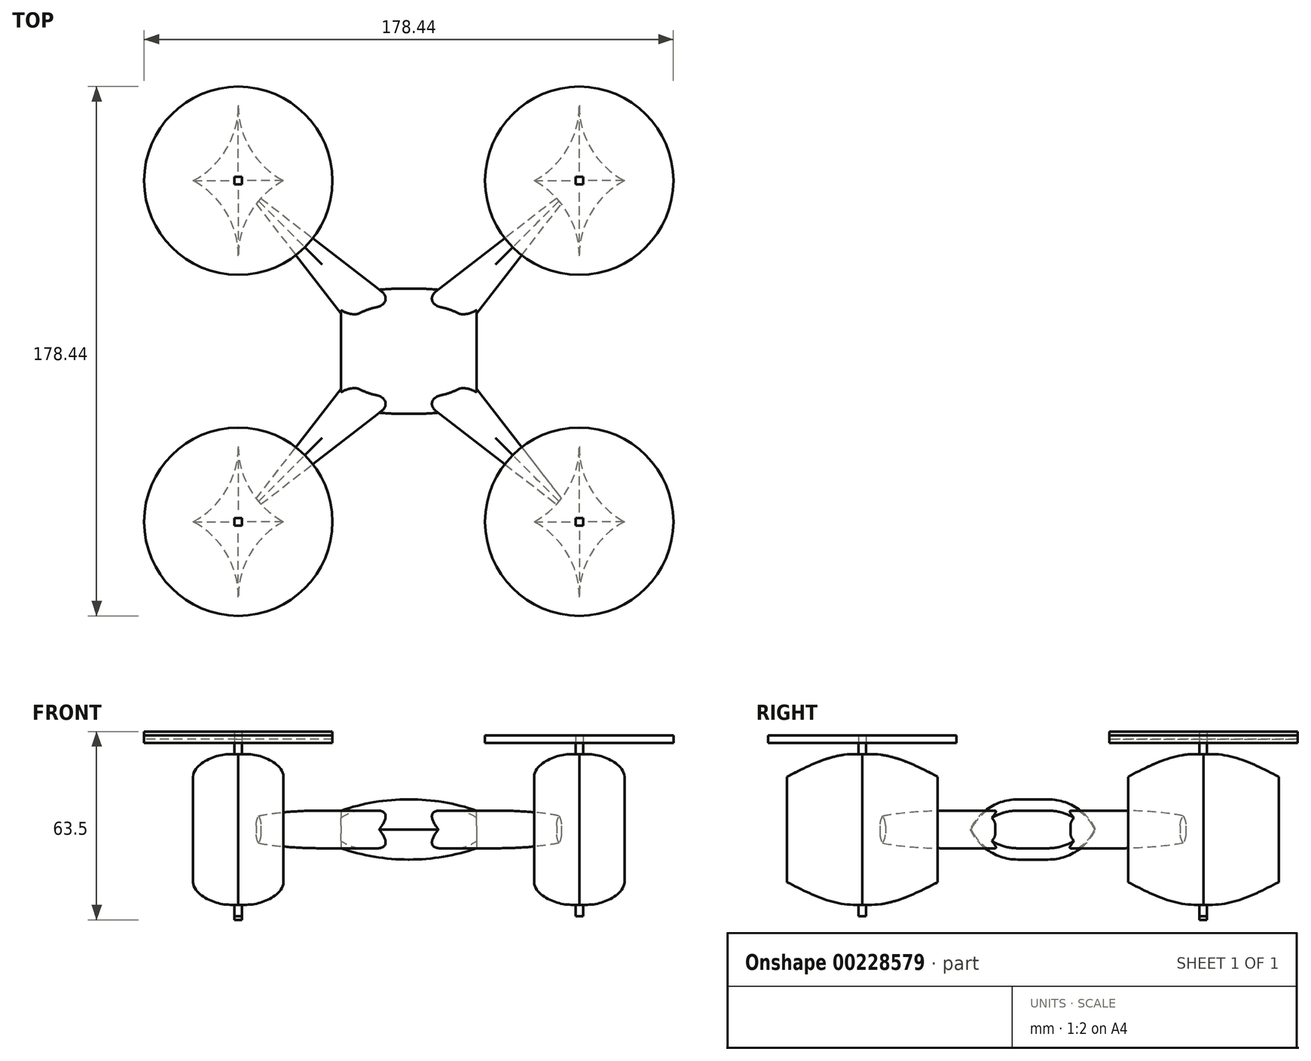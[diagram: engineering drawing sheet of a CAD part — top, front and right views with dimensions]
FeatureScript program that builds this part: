
annotation { "Feature Type Name" : "Feature", "Feature Type Description" : "" }
export const myFeature = defineFeature(function(context is Context, id is Id, definition is map)
    precondition{}
    {
        {
            var Q0;
            Q0=qCreatedBy(makeId("Top.planeOp"),FACE);
            var sketch = newSketch(context, id + "F0", { "sketchPlane" : qUnion([Q0])});
            skLineSegment(sketch, "E0.bottom", {"start": v(22.86, -22.86) * mm, "end": v(-22.86, -22.86) * mm});
            skLineSegment(sketch, "E0.top", {"start": v(22.86, 22.86) * mm, "end": v(-22.86, 22.86) * mm});
            skLineSegment(sketch, "E0.left", {"start": v(22.86, -22.86) * mm, "end": v(22.86, 22.86) * mm});
            skLineSegment(sketch, "E0.right", {"start": v(-22.86, -22.86) * mm, "end": v(-22.86, 22.86) * mm});
            skPoint(sketch, "E0.middle", {"position": v(0, 0) * mm});
            skLineSegment(sketch, "E1", {"start": v(0, 0) * mm, "end": v(-57.47, 57.47) * mm, "construction": true});
            skLineSegment(sketch, "E2", {"start": v(0, 0) * mm, "end": v(57.47, 57.47) * mm, "construction": true});
            skLineSegment(sketch, "E3", {"start": v(0, 0) * mm, "end": v(57.47, -57.47) * mm, "construction": true});
            skLineSegment(sketch, "E4", {"start": v(0, 0) * mm, "end": v(-57.47, -57.47) * mm, "construction": true});
            skLineSegment(sketch, "E5", {"start": v(-57.47, 57.47) * mm, "end": v(-57.47, 82.87) * mm, "construction": true});
            skLineSegment(sketch, "E6", {"start": v(-57.47, 32.07) * mm, "end": v(-57.47, 57.47) * mm, "construction": true});
            skLineSegment(sketch, "E7", {"start": v(-57.47, 57.47) * mm, "end": v(-42.23, 57.47) * mm, "construction": true});
            skLineSegment(sketch, "E8", {"start": v(-57.47, 57.47) * mm, "end": v(-72.71, 57.47) * mm, "construction": true});
            skArc(sketch, "E9", {"start": v(-72.71, 57.47) * mm, "mid": v(-61.58, 68.06) * mm, "end": v(-57.47, 82.87) * mm});
            skArc(sketch, "E10", {"start": v(-57.47, 82.87) * mm, "mid": v(-53.37, 68.06) * mm, "end": v(-42.23, 57.47) * mm});
            skArc(sketch, "E11", {"start": v(-57.47, 32.07) * mm, "mid": v(-61.58, 46.88) * mm, "end": v(-72.71, 57.47) * mm});
            skArc(sketch, "E12", {"start": v(-42.23, 57.47) * mm, "mid": v(-53.37, 46.88) * mm, "end": v(-57.47, 32.07) * mm});
            skLineSegment(sketch, "E13", {"start": v(57.47, 57.47) * mm, "end": v(57.47, 82.87) * mm, "construction": true});
            skLineSegment(sketch, "E14", {"start": v(57.47, 32.07) * mm, "end": v(57.47, 57.47) * mm, "construction": true});
            skLineSegment(sketch, "E15", {"start": v(57.47, 57.47) * mm, "end": v(72.71, 57.47) * mm, "construction": true});
            skLineSegment(sketch, "E16", {"start": v(57.47, 57.47) * mm, "end": v(42.23, 57.47) * mm, "construction": true});
            skArc(sketch, "E17", {"start": v(42.23, 57.47) * mm, "mid": v(53.37, 68.06) * mm, "end": v(57.47, 82.87) * mm});
            skArc(sketch, "E18", {"start": v(57.47, 82.87) * mm, "mid": v(61.58, 68.06) * mm, "end": v(72.71, 57.47) * mm});
            skArc(sketch, "E19", {"start": v(57.47, 32.07) * mm, "mid": v(53.37, 46.88) * mm, "end": v(42.23, 57.47) * mm});
            skArc(sketch, "E20", {"start": v(72.71, 57.47) * mm, "mid": v(61.58, 46.88) * mm, "end": v(57.47, 32.07) * mm});
            skLineSegment(sketch, "E21", {"start": v(57.47, -57.47) * mm, "end": v(57.47, -32.07) * mm, "construction": true});
            skLineSegment(sketch, "E22", {"start": v(57.47, -82.87) * mm, "end": v(57.47, -57.47) * mm, "construction": true});
            skLineSegment(sketch, "E23", {"start": v(57.47, -57.47) * mm, "end": v(72.71, -57.47) * mm, "construction": true});
            skLineSegment(sketch, "E24", {"start": v(57.47, -57.47) * mm, "end": v(42.23, -57.47) * mm, "construction": true});
            skArc(sketch, "E25", {"start": v(42.23, -57.47) * mm, "mid": v(53.37, -46.88) * mm, "end": v(57.47, -32.07) * mm});
            skArc(sketch, "E26", {"start": v(57.47, -32.07) * mm, "mid": v(61.58, -46.88) * mm, "end": v(72.71, -57.47) * mm});
            skArc(sketch, "E27", {"start": v(57.47, -82.87) * mm, "mid": v(53.37, -68.06) * mm, "end": v(42.23, -57.47) * mm});
            skArc(sketch, "E28", {"start": v(72.71, -57.47) * mm, "mid": v(61.58, -68.06) * mm, "end": v(57.47, -82.87) * mm});
            skLineSegment(sketch, "E29", {"start": v(-57.47, -57.47) * mm, "end": v(-57.47, -32.07) * mm, "construction": true});
            skLineSegment(sketch, "E30", {"start": v(-57.47, -82.87) * mm, "end": v(-57.47, -57.47) * mm, "construction": true});
            skLineSegment(sketch, "E31", {"start": v(-57.47, -57.47) * mm, "end": v(-42.23, -57.47) * mm, "construction": true});
            skLineSegment(sketch, "E32", {"start": v(-57.47, -57.47) * mm, "end": v(-72.71, -57.47) * mm, "construction": true});
            skArc(sketch, "E33", {"start": v(-72.71, -57.47) * mm, "mid": v(-61.58, -46.88) * mm, "end": v(-57.47, -32.07) * mm});
            skArc(sketch, "E34", {"start": v(-57.47, -32.07) * mm, "mid": v(-53.37, -46.88) * mm, "end": v(-42.23, -57.47) * mm});
            skArc(sketch, "E35", {"start": v(-57.47, -82.87) * mm, "mid": v(-61.58, -68.06) * mm, "end": v(-72.71, -57.47) * mm});
            skArc(sketch, "E36", {"start": v(-42.23, -57.47) * mm, "mid": v(-53.37, -68.06) * mm, "end": v(-57.47, -82.87) * mm});
            skLineSegment(sketch, "E37", {"start": v(0, 0) * mm, "end": v(-12.67, 22.86) * mm, "construction": true});
            skLineSegment(sketch, "E38", {"start": v(0, 0) * mm, "end": v(-22.86, 12.67) * mm, "construction": true});
            skLineSegment(sketch, "E39", {"start": v(0, 0) * mm, "end": v(12.67, 22.86) * mm, "construction": true});
            skLineSegment(sketch, "E40", {"start": v(0, 0) * mm, "end": v(22.86, 12.67) * mm, "construction": true});
            skLineSegment(sketch, "E41", {"start": v(0, 0) * mm, "end": v(-22.86, -12.67) * mm, "construction": true});
            skLineSegment(sketch, "E42", {"start": v(0, 0) * mm, "end": v(-12.67, -22.86) * mm, "construction": true});
            skLineSegment(sketch, "E43", {"start": v(0, 0) * mm, "end": v(22.86, -12.67) * mm, "construction": true});
            skLineSegment(sketch, "E44", {"start": v(0, 0) * mm, "end": v(12.67, -22.86) * mm, "construction": true});
            skLineSegment(sketch, "E45", {"start": v(-57.47, 57.47) * mm, "end": v(-12.67, 22.86) * mm});
            skLineSegment(sketch, "E46", {"start": v(-57.47, 57.47) * mm, "end": v(-22.86, 12.67) * mm});
            skLineSegment(sketch, "E47", {"start": v(57.47, 57.47) * mm, "end": v(12.67, 22.86) * mm});
            skLineSegment(sketch, "E48", {"start": v(22.86, 12.67) * mm, "end": v(57.47, 57.47) * mm});
            skLineSegment(sketch, "E49", {"start": v(22.86, -12.67) * mm, "end": v(57.47, -57.47) * mm});
            skLineSegment(sketch, "E50", {"start": v(12.67, -22.86) * mm, "end": v(57.47, -57.47) * mm});
            skLineSegment(sketch, "E51", {"start": v(-57.47, -57.47) * mm, "end": v(-22.86, -12.67) * mm});
            skLineSegment(sketch, "E52", {"start": v(-57.47, -57.47) * mm, "end": v(-12.67, -22.86) * mm});
            skLineSegment(sketch, "E53", {"start": v(22.86, 0) * mm, "end": v(-22.86, 0) * mm, "construction": true});
            skLineSegment(sketch, "E54.bottom", {"start": v(-58.74, 56.2) * mm, "end": v(-56.2, 56.2) * mm});
            skLineSegment(sketch, "E54.top", {"start": v(-58.74, 58.74) * mm, "end": v(-56.2, 58.74) * mm});
            skLineSegment(sketch, "E54.left", {"start": v(-58.74, 56.2) * mm, "end": v(-58.74, 58.74) * mm});
            skLineSegment(sketch, "E54.right", {"start": v(-56.2, 56.2) * mm, "end": v(-56.2, 58.74) * mm});
            skPoint(sketch, "E54.middle", {"position": v(-57.47, 57.47) * mm});
            skLineSegment(sketch, "E55.bottom", {"start": v(58.74, 58.74) * mm, "end": v(56.2, 58.74) * mm});
            skLineSegment(sketch, "E55.top", {"start": v(58.74, 56.2) * mm, "end": v(56.2, 56.2) * mm});
            skLineSegment(sketch, "E55.left", {"start": v(58.74, 58.74) * mm, "end": v(58.74, 56.2) * mm});
            skLineSegment(sketch, "E55.right", {"start": v(56.2, 58.74) * mm, "end": v(56.2, 56.2) * mm});
            skPoint(sketch, "E55.middle", {"position": v(57.47, 57.47) * mm});
            skLineSegment(sketch, "E56.bottom", {"start": v(58.74, -58.74) * mm, "end": v(56.2, -58.74) * mm});
            skLineSegment(sketch, "E56.top", {"start": v(58.74, -56.2) * mm, "end": v(56.2, -56.2) * mm});
            skLineSegment(sketch, "E56.left", {"start": v(58.74, -58.74) * mm, "end": v(58.74, -56.2) * mm});
            skLineSegment(sketch, "E56.right", {"start": v(56.2, -58.74) * mm, "end": v(56.2, -56.2) * mm});
            skPoint(sketch, "E56.middle", {"position": v(57.47, -57.47) * mm});
            skLineSegment(sketch, "E57.bottom", {"start": v(-58.74, -58.74) * mm, "end": v(-56.2, -58.74) * mm});
            skLineSegment(sketch, "E57.top", {"start": v(-58.74, -56.2) * mm, "end": v(-56.2, -56.2) * mm});
            skLineSegment(sketch, "E57.left", {"start": v(-58.74, -58.74) * mm, "end": v(-58.74, -56.2) * mm});
            skLineSegment(sketch, "E57.right", {"start": v(-56.2, -58.74) * mm, "end": v(-56.2, -56.2) * mm});
            skPoint(sketch, "E57.middle", {"position": v(-57.47, -57.47) * mm});
            skSolve(sketch);
        }
        {
            var Q0;
            {var subQ0=sQuery(id+"F0.wireOp",EDGE,"E0.left");var subQ3=sQuery(id+"F0.wireOp",EDGE,"E0.bottom");var subQ4=makeQuery(id+"F0.imprint","INTERSECT",VERTEX,{"derivedFrom":[subQ3,subQ0]});Q0=makeQuery(id+"F0.imprint","IMPRINT",FACE,{"disambiguationData":[TD([[makeQuery(id+"F0.imprint","IMPRINT",EDGE,{"disambiguationData":[TD([[subQ4,-1.0]])],"derivedFrom":subQ3}),-1.0]])]});}
            extrude(context, id + "F1", {"entities" : qUnion([Q0]), "endBound" : BoundingType.SYMMETRIC, "depth" : 20.32 * mm});
        }
        {
            var Q0;
            {var subQ5=sQuery(id+"F0.wireOp",EDGE,"E0.right");var subQ6=sQuery(id+"F0.wireOp",EDGE,"E0.top");var subQ7=makeQuery(id+"F0.imprint","INTERSECT",VERTEX,{"derivedFrom":[subQ6,subQ5]});Q0=makeQuery(id+"F0.imprint","IMPRINT",FACE,{"disambiguationData":[TD([[makeQuery(id+"F0.imprint","IMPRINT",EDGE,{"disambiguationData":[TD([[subQ7,1.0]])],"derivedFrom":subQ6}),-1.0]])]});}
            var Q1;
            {var subQ5=sQuery(id+"F0.wireOp",EDGE,"E0.left");var subQ6=sQuery(id+"F0.wireOp",EDGE,"E0.top");var subQ7=makeQuery(id+"F0.imprint","INTERSECT",VERTEX,{"derivedFrom":[subQ6,subQ5]});Q1=makeQuery(id+"F0.imprint","IMPRINT",FACE,{"disambiguationData":[TD([[makeQuery(id+"F0.imprint","IMPRINT",EDGE,{"disambiguationData":[TD([[subQ7,-1.0]])],"derivedFrom":subQ6}),-1.0]])]});}
            var Q2;
            {var subQ1=sQuery(id+"F0.wireOp",EDGE,"E0.left");var subQ5=sQuery(id+"F0.wireOp",EDGE,"E0.bottom");var subQ6=makeQuery(id+"F0.imprint","INTERSECT",VERTEX,{"derivedFrom":[subQ5,subQ1]});Q2=makeQuery(id+"F0.imprint","IMPRINT",FACE,{"disambiguationData":[TD([[makeQuery(id+"F0.imprint","IMPRINT",EDGE,{"disambiguationData":[TD([[subQ6,-1.0]])],"derivedFrom":subQ5}),1.0]])]});}
            var Q3;
            {var subQ1=sQuery(id+"F0.wireOp",EDGE,"E0.right");var subQ5=sQuery(id+"F0.wireOp",EDGE,"E0.bottom");var subQ6=makeQuery(id+"F0.imprint","INTERSECT",VERTEX,{"derivedFrom":[subQ5,subQ1]});Q3=makeQuery(id+"F0.imprint","IMPRINT",FACE,{"disambiguationData":[TD([[makeQuery(id+"F0.imprint","IMPRINT",EDGE,{"disambiguationData":[TD([[subQ6,1.0]])],"derivedFrom":subQ5}),1.0]])]});}
            extrude(context, id + "F2", {"entities" : qUnion([Q0, Q1, Q2, Q3]), "operationType" : NewBodyOperationType.ADD, "endBound" : BoundingType.SYMMETRIC, "depth" : 12.7 * mm});
        }
        {
            var Q0;
            Q0=makeQuery(id+"F0.imprint","IMPRINT",FACE,{"disambiguationData":[TD([[makeQuery(id+"F0.imprint","IMPRINT",EDGE,{"derivedFrom":sQuery(id+"F0.wireOp",EDGE,"E9")}),-1.0]])]});
            var Q1;
            {var subQ0=sQuery(id+"F0.wireOp",EDGE,"E45");var subQ1=sQuery(id+"F0.wireOp",EDGE,"E12");var subQ2=makeQuery(id+"F0.imprint","INTERSECT",VERTEX,{"derivedFrom":[subQ1,subQ0]});Q1=makeQuery(id+"F0.imprint","IMPRINT",FACE,{"disambiguationData":[TD([[makeQuery(id+"F0.imprint","IMPRINT",EDGE,{"disambiguationData":[TD([[subQ2,-1.0]])],"derivedFrom":subQ1}),-1.0]])]});}
            var Q2;
            {var subQ1=sQuery(id+"F0.wireOp",EDGE,"E17");Q2=makeQuery(id+"F0.imprint","IMPRINT",FACE,{"disambiguationData":[TD([[makeQuery(id+"F0.imprint","IMPRINT",EDGE,{"derivedFrom":subQ1}),-1.0]])]});}
            var Q3;
            {var subQ0=sQuery(id+"F0.wireOp",EDGE,"E48");var subQ1=sQuery(id+"F0.wireOp",EDGE,"E19");var subQ2=makeQuery(id+"F0.imprint","INTERSECT",VERTEX,{"derivedFrom":[subQ1,subQ0]});Q3=makeQuery(id+"F0.imprint","IMPRINT",FACE,{"disambiguationData":[TD([[makeQuery(id+"F0.imprint","IMPRINT",EDGE,{"disambiguationData":[TD([[subQ2,-1.0]])],"derivedFrom":subQ1}),-1.0]])]});}
            var Q4;
            {var subQ1=sQuery(id+"F0.wireOp",EDGE,"E26");Q4=makeQuery(id+"F0.imprint","IMPRINT",FACE,{"disambiguationData":[TD([[makeQuery(id+"F0.imprint","IMPRINT",EDGE,{"derivedFrom":subQ1}),-1.0]])]});}
            var Q5;
            {var subQ0=sQuery(id+"F0.wireOp",EDGE,"E50");var subQ1=sQuery(id+"F0.wireOp",EDGE,"E25");var subQ2=makeQuery(id+"F0.imprint","INTERSECT",VERTEX,{"derivedFrom":[subQ1,subQ0]});Q5=makeQuery(id+"F0.imprint","IMPRINT",FACE,{"disambiguationData":[TD([[makeQuery(id+"F0.imprint","IMPRINT",EDGE,{"disambiguationData":[TD([[subQ2,-1.0]])],"derivedFrom":subQ1}),-1.0]])]});}
            var Q6;
            {var subQ4=sQuery(id+"F0.wireOp",EDGE,"E33");Q6=makeQuery(id+"F0.imprint","IMPRINT",FACE,{"disambiguationData":[TD([[makeQuery(id+"F0.imprint","IMPRINT",EDGE,{"derivedFrom":subQ4}),-1.0]])]});}
            var Q7;
            {var subQ0=sQuery(id+"F0.wireOp",EDGE,"E51");var subQ1=sQuery(id+"F0.wireOp",EDGE,"E34");var subQ2=makeQuery(id+"F0.imprint","INTERSECT",VERTEX,{"derivedFrom":[subQ1,subQ0]});Q7=makeQuery(id+"F0.imprint","IMPRINT",FACE,{"disambiguationData":[TD([[makeQuery(id+"F0.imprint","IMPRINT",EDGE,{"disambiguationData":[TD([[subQ2,-1.0]])],"derivedFrom":subQ1}),-1.0]])]});}
            extrude(context, id + "F3", {"entities" : qUnion([Q0, Q1, Q2, Q3, Q4, Q5, Q6, Q7]), "operationType" : NewBodyOperationType.ADD, "endBound" : BoundingType.SYMMETRIC, "depth" : 50.8 * mm});
        }
        {
            var Q0;
            Q0=makeQuery(id+"F2.opExtrude","CAP_EDGE",EDGE,{"disambiguationData":[OSD([sQuery(id+"F0.wireOp",EDGE,"E50")])],"isStart":false});
            var Q1;
            Q1=makeQuery(id+"F2.opExtrude","CAP_EDGE",EDGE,{"disambiguationData":[OSD([sQuery(id+"F0.wireOp",EDGE,"E49")])],"isStart":false});
            var Q2;
            Q2=makeQuery(id+"F2.opExtrude","CAP_EDGE",EDGE,{"disambiguationData":[OSD([sQuery(id+"F0.wireOp",EDGE,"E50")])],"isStart":true});
            var Q3;
            Q3=makeQuery(id+"F2.opExtrude","CAP_EDGE",EDGE,{"disambiguationData":[OSD([sQuery(id+"F0.wireOp",EDGE,"E49")])],"isStart":true});
            fillet(context, id + "F4", {"entities" : qUnion([Q0, Q1, Q2, Q3]), "radius" : 5.08 * mm, "tangentPropagation" : true, "allowEdgeOverflow" : false});
        }
        {
            var Q0;
            Q0=makeQuery(id+"F2.opExtrude","CAP_EDGE",EDGE,{"disambiguationData":[OSD([sQuery(id+"F0.wireOp",EDGE,"E52")])],"isStart":false});
            var Q1;
            Q1=makeQuery(id+"F2.opExtrude","CAP_EDGE",EDGE,{"disambiguationData":[OSD([sQuery(id+"F0.wireOp",EDGE,"E51")])],"isStart":false});
            var Q2;
            Q2=makeQuery(id+"F2.opExtrude","CAP_EDGE",EDGE,{"disambiguationData":[OSD([sQuery(id+"F0.wireOp",EDGE,"E51")])],"isStart":true});
            var Q3;
            Q3=makeQuery(id+"F2.opExtrude","CAP_EDGE",EDGE,{"disambiguationData":[OSD([sQuery(id+"F0.wireOp",EDGE,"E52")])],"isStart":true});
            var Q4;
            Q4=makeQuery(id+"F2.opExtrude","CAP_EDGE",EDGE,{"disambiguationData":[OSD([sQuery(id+"F0.wireOp",EDGE,"E48")])],"isStart":false});
            var Q5;
            Q5=makeQuery(id+"F2.opExtrude","CAP_EDGE",EDGE,{"disambiguationData":[OSD([sQuery(id+"F0.wireOp",EDGE,"E47")])],"isStart":false});
            var Q6;
            Q6=makeQuery(id+"F2.opExtrude","CAP_EDGE",EDGE,{"disambiguationData":[OSD([sQuery(id+"F0.wireOp",EDGE,"E48")])],"isStart":true});
            var Q7;
            Q7=makeQuery(id+"F2.opExtrude","CAP_EDGE",EDGE,{"disambiguationData":[OSD([sQuery(id+"F0.wireOp",EDGE,"E47")])],"isStart":true});
            var Q8;
            Q8=makeQuery(id+"F2.opExtrude","CAP_EDGE",EDGE,{"disambiguationData":[OSD([sQuery(id+"F0.wireOp",EDGE,"E45")])],"isStart":true});
            var Q9;
            Q9=makeQuery(id+"F2.opExtrude","CAP_EDGE",EDGE,{"disambiguationData":[OSD([sQuery(id+"F0.wireOp",EDGE,"E46")])],"isStart":true});
            var Q10;
            Q10=makeQuery(id+"F2.opExtrude","CAP_EDGE",EDGE,{"disambiguationData":[OSD([sQuery(id+"F0.wireOp",EDGE,"E46")])],"isStart":false});
            var Q11;
            Q11=makeQuery(id+"F2.opExtrude","CAP_EDGE",EDGE,{"disambiguationData":[OSD([sQuery(id+"F0.wireOp",EDGE,"E45")])],"isStart":false});
            fillet(context, id + "F5", {"entities" : qUnion([Q0, Q1, Q2, Q3, Q4, Q5, Q6, Q7, Q8, Q9, Q10, Q11]), "radius" : 5.08 * mm, "tangentPropagation" : true, "allowEdgeOverflow" : false});
        }
        {
            var Q0;
            Q0=makeQuery(id+"F1.opExtrude","CAP_EDGE",EDGE,{"disambiguationData":[OSD([sQuery(id+"F0.wireOp",EDGE,"E0.right")])],"isStart":true});
            var Q1;
            Q1=makeQuery(id+"F1.opExtrude","CAP_EDGE",EDGE,{"disambiguationData":[OSD([sQuery(id+"F0.wireOp",EDGE,"E0.right")])],"isStart":false});
            fillet(context, id + "F6", {"entities" : qUnion([Q0, Q1]), "radius" : 69.9 * mm, "tangentPropagation" : true, "allowEdgeOverflow" : false});
        }
        {
            var Q0;
            Q0=makeQuery(id+"F1.opExtrude","CAP_EDGE",EDGE,{"disambiguationData":[OSD([sQuery(id+"F0.wireOp",EDGE,"E0.left")])],"isStart":true});
            var Q1;
            Q1=makeQuery(id+"F1.opExtrude","CAP_EDGE",EDGE,{"disambiguationData":[OSD([sQuery(id+"F0.wireOp",EDGE,"E0.left")])],"isStart":false});
            fillet(context, id + "F7", {"entities" : qUnion([Q0, Q1]), "radius" : 69.9 * mm, "tangentPropagation" : true, "allowEdgeOverflow" : false});
        }
        {
            var Q0;
            Q0=makeQuery(id+"F6.opFillet","BLEND_EDGE",EDGE,{"blendedFrom":[makeQuery(id+"F1.opExtrude","CAP_EDGE",EDGE,{"disambiguationData":[OSD([sQuery(id+"F0.wireOp",EDGE,"E0.right")])],"isStart":false}),makeQuery(id+"F1.opExtrude","SWEPT_FACE",FACE,{"disambiguationData":[OSD([sQuery(id+"F0.wireOp",EDGE,"E0.bottom")])]})],"blendedInto":[makeQuery(id+"F1.opExtrude","SWEPT_FACE",FACE,{"disambiguationData":[OSD([sQuery(id+"F0.wireOp",EDGE,"E0.bottom")])]})]});
            var Q1;
            Q1=makeQuery(id+"F7.opFillet","BLEND_EDGE",EDGE,{"blendedFrom":[makeQuery(id+"F1.opExtrude","CAP_EDGE",EDGE,{"disambiguationData":[OSD([sQuery(id+"F0.wireOp",EDGE,"E0.left")])],"isStart":false}),makeQuery(id+"F1.opExtrude","SWEPT_FACE",FACE,{"disambiguationData":[OSD([sQuery(id+"F0.wireOp",EDGE,"E0.bottom")])]})],"blendedInto":[makeQuery(id+"F1.opExtrude","SWEPT_FACE",FACE,{"disambiguationData":[OSD([sQuery(id+"F0.wireOp",EDGE,"E0.bottom")])]})]});
            var Q2;
            Q2=makeQuery(id+"F7.opFillet","BLEND_EDGE",EDGE,{"blendedFrom":[makeQuery(id+"F1.opExtrude","CAP_EDGE",EDGE,{"disambiguationData":[OSD([sQuery(id+"F0.wireOp",EDGE,"E0.left")])],"isStart":true}),makeQuery(id+"F1.opExtrude","SWEPT_FACE",FACE,{"disambiguationData":[OSD([sQuery(id+"F0.wireOp",EDGE,"E0.bottom")])]})],"blendedInto":[makeQuery(id+"F1.opExtrude","SWEPT_FACE",FACE,{"disambiguationData":[OSD([sQuery(id+"F0.wireOp",EDGE,"E0.bottom")])]})]});
            var Q3;
            Q3=makeQuery(id+"F6.opFillet","BLEND_EDGE",EDGE,{"blendedFrom":[makeQuery(id+"F1.opExtrude","CAP_EDGE",EDGE,{"disambiguationData":[OSD([sQuery(id+"F0.wireOp",EDGE,"E0.right")])],"isStart":true}),makeQuery(id+"F1.opExtrude","SWEPT_FACE",FACE,{"disambiguationData":[OSD([sQuery(id+"F0.wireOp",EDGE,"E0.bottom")])]})],"blendedInto":[makeQuery(id+"F1.opExtrude","SWEPT_FACE",FACE,{"disambiguationData":[OSD([sQuery(id+"F0.wireOp",EDGE,"E0.bottom")])]})]});
            fillet(context, id + "F8", {"entities" : qUnion([Q0, Q1, Q2, Q3]), "radius" : 17.78 * mm, "tangentPropagation" : true, "allowEdgeOverflow" : false});
        }
        {
            var Q0;
            Q0=makeQuery(id+"F7.opFillet","BLEND_EDGE",EDGE,{"blendedFrom":[makeQuery(id+"F1.opExtrude","CAP_EDGE",EDGE,{"disambiguationData":[OSD([sQuery(id+"F0.wireOp",EDGE,"E0.left")])],"isStart":true}),makeQuery(id+"F1.opExtrude","SWEPT_FACE",FACE,{"disambiguationData":[OSD([sQuery(id+"F0.wireOp",EDGE,"E0.top")])]})],"blendedInto":[makeQuery(id+"F1.opExtrude","SWEPT_FACE",FACE,{"disambiguationData":[OSD([sQuery(id+"F0.wireOp",EDGE,"E0.top")])]})]});
            var Q1;
            Q1=makeQuery(id+"F6.opFillet","BLEND_EDGE",EDGE,{"blendedFrom":[makeQuery(id+"F1.opExtrude","CAP_EDGE",EDGE,{"disambiguationData":[OSD([sQuery(id+"F0.wireOp",EDGE,"E0.right")])],"isStart":false}),makeQuery(id+"F1.opExtrude","SWEPT_FACE",FACE,{"disambiguationData":[OSD([sQuery(id+"F0.wireOp",EDGE,"E0.top")])]})],"blendedInto":[makeQuery(id+"F1.opExtrude","SWEPT_FACE",FACE,{"disambiguationData":[OSD([sQuery(id+"F0.wireOp",EDGE,"E0.top")])]})]});
            var Q2;
            Q2=makeQuery(id+"F7.opFillet","BLEND_EDGE",EDGE,{"blendedFrom":[makeQuery(id+"F1.opExtrude","CAP_EDGE",EDGE,{"disambiguationData":[OSD([sQuery(id+"F0.wireOp",EDGE,"E0.left")])],"isStart":false}),makeQuery(id+"F1.opExtrude","SWEPT_FACE",FACE,{"disambiguationData":[OSD([sQuery(id+"F0.wireOp",EDGE,"E0.top")])]})],"blendedInto":[makeQuery(id+"F1.opExtrude","SWEPT_FACE",FACE,{"disambiguationData":[OSD([sQuery(id+"F0.wireOp",EDGE,"E0.top")])]})]});
            fillet(context, id + "F9", {"entities" : qUnion([Q0, Q1, Q2]), "radius" : 17.78 * mm, "tangentPropagation" : true, "allowEdgeOverflow" : false});
        }
        {
            var Q0;
            Q0=makeQuery(id+"F3.opExtrude","CAP_EDGE",EDGE,{"disambiguationData":[OSD([sQuery(id+"F0.wireOp",EDGE,"E9")])],"isStart":false});
            var Q1;
            Q1=makeQuery(id+"F3.opExtrude","CAP_EDGE",EDGE,{"disambiguationData":[OSD([sQuery(id+"F0.wireOp",EDGE,"E10")])],"isStart":false});
            var Q2;
            Q2=makeQuery(id+"F3.opExtrude","CAP_EDGE",EDGE,{"disambiguationData":[OSD([sQuery(id+"F0.wireOp",EDGE,"E12")])],"isStart":false});
            var Q3;
            Q3=makeQuery(id+"F3.opExtrude","CAP_EDGE",EDGE,{"disambiguationData":[OSD([sQuery(id+"F0.wireOp",EDGE,"E11")])],"isStart":false});
            fillet(context, id + "F10", {"entities" : qUnion([Q0, Q1, Q2, Q3]), "radius" : 7.62 * mm, "tangentPropagation" : true, "allowEdgeOverflow" : false});
        }
        {
            var Q0;
            Q0=makeQuery(id+"F3.opExtrude","CAP_EDGE",EDGE,{"disambiguationData":[OSD([sQuery(id+"F0.wireOp",EDGE,"E17")])],"isStart":false});
            var Q1;
            Q1=makeQuery(id+"F3.opExtrude","CAP_EDGE",EDGE,{"disambiguationData":[OSD([sQuery(id+"F0.wireOp",EDGE,"E18")])],"isStart":false});
            var Q2;
            Q2=makeQuery(id+"F3.opExtrude","CAP_EDGE",EDGE,{"disambiguationData":[OSD([sQuery(id+"F0.wireOp",EDGE,"E19")])],"isStart":false});
            var Q3;
            Q3=makeQuery(id+"F3.opExtrude","CAP_EDGE",EDGE,{"disambiguationData":[OSD([sQuery(id+"F0.wireOp",EDGE,"E20")])],"isStart":false});
            var Q4;
            Q4=makeQuery(id+"F3.opExtrude","CAP_EDGE",EDGE,{"disambiguationData":[OSD([sQuery(id+"F0.wireOp",EDGE,"E25")])],"isStart":false});
            var Q5;
            Q5=makeQuery(id+"F3.opExtrude","CAP_EDGE",EDGE,{"disambiguationData":[OSD([sQuery(id+"F0.wireOp",EDGE,"E26")])],"isStart":false});
            var Q6;
            Q6=makeQuery(id+"F3.opExtrude","CAP_EDGE",EDGE,{"disambiguationData":[OSD([sQuery(id+"F0.wireOp",EDGE,"E28")])],"isStart":false});
            var Q7;
            Q7=makeQuery(id+"F3.opExtrude","CAP_EDGE",EDGE,{"disambiguationData":[OSD([sQuery(id+"F0.wireOp",EDGE,"E27")])],"isStart":false});
            var Q8;
            Q8=makeQuery(id+"F3.opExtrude","CAP_EDGE",EDGE,{"disambiguationData":[OSD([sQuery(id+"F0.wireOp",EDGE,"E34")])],"isStart":false});
            var Q9;
            Q9=makeQuery(id+"F3.opExtrude","CAP_EDGE",EDGE,{"disambiguationData":[OSD([sQuery(id+"F0.wireOp",EDGE,"E33")])],"isStart":false});
            var Q10;
            Q10=makeQuery(id+"F3.opExtrude","CAP_EDGE",EDGE,{"disambiguationData":[OSD([sQuery(id+"F0.wireOp",EDGE,"E35")])],"isStart":false});
            var Q11;
            Q11=makeQuery(id+"F3.opExtrude","CAP_EDGE",EDGE,{"disambiguationData":[OSD([sQuery(id+"F0.wireOp",EDGE,"E36")])],"isStart":false});
            fillet(context, id + "F11", {"entities" : qUnion([Q0, Q1, Q2, Q3, Q4, Q5, Q6, Q7, Q8, Q9, Q10, Q11]), "radius" : 7.62 * mm, "tangentPropagation" : true, "allowEdgeOverflow" : false});
        }
        {
            var Q0;
            Q0=makeQuery(id+"F3.opExtrude","CAP_EDGE",EDGE,{"disambiguationData":[OSD([sQuery(id+"F0.wireOp",EDGE,"E33")])],"isStart":true});
            var Q1;
            Q1=makeQuery(id+"F3.opExtrude","CAP_EDGE",EDGE,{"disambiguationData":[OSD([sQuery(id+"F0.wireOp",EDGE,"E34")])],"isStart":true});
            var Q2;
            Q2=makeQuery(id+"F3.opExtrude","CAP_EDGE",EDGE,{"disambiguationData":[OSD([sQuery(id+"F0.wireOp",EDGE,"E35")])],"isStart":true});
            var Q3;
            Q3=makeQuery(id+"F3.opExtrude","CAP_EDGE",EDGE,{"disambiguationData":[OSD([sQuery(id+"F0.wireOp",EDGE,"E36")])],"isStart":true});
            fillet(context, id + "F12", {"entities" : qUnion([Q0, Q1, Q2, Q3]), "radius" : 7.62 * mm, "tangentPropagation" : true, "allowEdgeOverflow" : false});
        }
        {
            var Q0;
            Q0=makeQuery(id+"F3.opExtrude","CAP_EDGE",EDGE,{"disambiguationData":[OSD([sQuery(id+"F0.wireOp",EDGE,"E27")])],"isStart":true});
            var Q1;
            Q1=makeQuery(id+"F3.opExtrude","CAP_EDGE",EDGE,{"disambiguationData":[OSD([sQuery(id+"F0.wireOp",EDGE,"E28")])],"isStart":true});
            var Q2;
            Q2=makeQuery(id+"F3.opExtrude","CAP_EDGE",EDGE,{"disambiguationData":[OSD([sQuery(id+"F0.wireOp",EDGE,"E26")])],"isStart":true});
            var Q3;
            Q3=makeQuery(id+"F3.opExtrude","CAP_EDGE",EDGE,{"disambiguationData":[OSD([sQuery(id+"F0.wireOp",EDGE,"E25")])],"isStart":true});
            var Q4;
            Q4=makeQuery(id+"F3.opExtrude","CAP_EDGE",EDGE,{"disambiguationData":[OSD([sQuery(id+"F0.wireOp",EDGE,"E20")])],"isStart":true});
            var Q5;
            Q5=makeQuery(id+"F3.opExtrude","CAP_EDGE",EDGE,{"disambiguationData":[OSD([sQuery(id+"F0.wireOp",EDGE,"E19")])],"isStart":true});
            var Q6;
            Q6=makeQuery(id+"F3.opExtrude","CAP_EDGE",EDGE,{"disambiguationData":[OSD([sQuery(id+"F0.wireOp",EDGE,"E17")])],"isStart":true});
            var Q7;
            Q7=makeQuery(id+"F3.opExtrude","CAP_EDGE",EDGE,{"disambiguationData":[OSD([sQuery(id+"F0.wireOp",EDGE,"E18")])],"isStart":true});
            var Q8;
            Q8=makeQuery(id+"F3.opExtrude","CAP_EDGE",EDGE,{"disambiguationData":[OSD([sQuery(id+"F0.wireOp",EDGE,"E12")])],"isStart":true});
            var Q9;
            Q9=makeQuery(id+"F3.opExtrude","CAP_EDGE",EDGE,{"disambiguationData":[OSD([sQuery(id+"F0.wireOp",EDGE,"E11")])],"isStart":true});
            var Q10;
            Q10=makeQuery(id+"F3.opExtrude","CAP_EDGE",EDGE,{"disambiguationData":[OSD([sQuery(id+"F0.wireOp",EDGE,"E9")])],"isStart":true});
            var Q11;
            Q11=makeQuery(id+"F3.opExtrude","CAP_EDGE",EDGE,{"disambiguationData":[OSD([sQuery(id+"F0.wireOp",EDGE,"E10")])],"isStart":true});
            fillet(context, id + "F13", {"entities" : qUnion([Q0, Q1, Q2, Q3, Q4, Q5, Q6, Q7, Q8, Q9, Q10, Q11]), "radius" : 7.62 * mm, "tangentPropagation" : true, "allowEdgeOverflow" : false});
        }
        {
            var Q0;
            {var subQ0=sQuery(id+"F0.wireOp",EDGE,"E54.top");Q0=makeQuery(id+"F0.imprint","IMPRINT",FACE,{"disambiguationData":[TD([[makeQuery(id+"F0.imprint","IMPRINT",EDGE,{"derivedFrom":subQ0}),-1.0]])]});}
            var Q1;
            {var subQ0=sQuery(id+"F0.wireOp",EDGE,"E46");var subQ1=sQuery(id+"F0.wireOp",EDGE,"E45");var subQ2=makeQuery(id+"F0.imprint","INTERSECT",VERTEX,{"derivedFrom":[subQ1,subQ0]});Q1=makeQuery(id+"F0.imprint","IMPRINT",FACE,{"disambiguationData":[TD([[makeQuery(id+"F0.imprint","IMPRINT",EDGE,{"disambiguationData":[TD([[subQ2,-1.0]])],"derivedFrom":subQ1}),-1.0]])]});}
            extrude(context, id + "F14", {"entities" : qUnion([Q0, Q1]), "operationType" : NewBodyOperationType.ADD, "endBound" : BoundingType.SYMMETRIC, "depth" : 60.96 * mm});
        }
        {
            var Q0;
            {var subQ4=sQuery(id+"F0.wireOp",EDGE,"E57.bottom");Q0=makeQuery(id+"F0.imprint","IMPRINT",FACE,{"disambiguationData":[TD([[makeQuery(id+"F0.imprint","IMPRINT",EDGE,{"derivedFrom":subQ4}),1.0]])]});}
            var Q1;
            {var subQ0=sQuery(id+"F0.wireOp",EDGE,"E52");var subQ1=sQuery(id+"F0.wireOp",EDGE,"E51");var subQ2=makeQuery(id+"F0.imprint","INTERSECT",VERTEX,{"derivedFrom":[subQ1,subQ0]});Q1=makeQuery(id+"F0.imprint","IMPRINT",FACE,{"disambiguationData":[TD([[makeQuery(id+"F0.imprint","IMPRINT",EDGE,{"disambiguationData":[TD([[subQ2,-1.0]])],"derivedFrom":subQ1}),-1.0]])]});}
            var Q2;
            {var subQ4=sQuery(id+"F0.wireOp",EDGE,"E56.bottom");Q2=makeQuery(id+"F0.imprint","IMPRINT",FACE,{"disambiguationData":[TD([[makeQuery(id+"F0.imprint","IMPRINT",EDGE,{"derivedFrom":subQ4}),-1.0]])]});}
            var Q3;
            {var subQ0=sQuery(id+"F0.wireOp",EDGE,"E50");var subQ1=sQuery(id+"F0.wireOp",EDGE,"E49");var subQ2=makeQuery(id+"F0.imprint","INTERSECT",VERTEX,{"derivedFrom":[subQ1,subQ0]});Q3=makeQuery(id+"F0.imprint","IMPRINT",FACE,{"disambiguationData":[TD([[makeQuery(id+"F0.imprint","IMPRINT",EDGE,{"disambiguationData":[TD([[subQ2,1.0]])],"derivedFrom":subQ1}),-1.0]])]});}
            var Q4;
            {var subQ4=sQuery(id+"F0.wireOp",EDGE,"E55.bottom");Q4=makeQuery(id+"F0.imprint","IMPRINT",FACE,{"disambiguationData":[TD([[makeQuery(id+"F0.imprint","IMPRINT",EDGE,{"derivedFrom":subQ4}),1.0]])]});}
            var Q5;
            {var subQ0=sQuery(id+"F0.wireOp",EDGE,"E48");var subQ1=sQuery(id+"F0.wireOp",EDGE,"E47");var subQ2=makeQuery(id+"F0.imprint","INTERSECT",VERTEX,{"derivedFrom":[subQ1,subQ0]});Q5=makeQuery(id+"F0.imprint","IMPRINT",FACE,{"disambiguationData":[TD([[makeQuery(id+"F0.imprint","IMPRINT",EDGE,{"disambiguationData":[TD([[subQ2,-1.0]])],"derivedFrom":subQ1}),1.0]])]});}
            extrude(context, id + "F15", {"entities" : qUnion([Q0, Q1, Q2, Q3, Q4, Q5]), "operationType" : NewBodyOperationType.ADD, "endBound" : BoundingType.SYMMETRIC, "depth" : 58.42 * mm});
        }
        {
            var Q0;
            Q0=makeQuery(id+"F14.opExtrude","CAP_FACE",FACE,{"disambiguationData":[OSD([sQuery(id+"F0.wireOp",EDGE,"E54.bottom"),sQuery(id+"F0.wireOp",EDGE,"E54.top"),sQuery(id+"F0.wireOp",EDGE,"E54.left"),sQuery(id+"F0.wireOp",EDGE,"E54.right")])],"isStart":false});
            var sketch = newSketch(context, id + "F16", { "sketchPlane" : qUnion([Q0])});
            skLineSegment(sketch, "E58", {"start": v(-57.47, 58.74) * mm, "end": v(-57.47, 56.2) * mm, "construction": true});
            skCircle(sketch, "E59", {"center": v(-57.47, 57.47) * mm, "radius": 31.75 * mm});
            skSolve(sketch);
        }
        {
            var Q0;
            Q0=makeQuery(id+"F15.opExtrude","CAP_FACE",FACE,{"disambiguationData":[OSD([sQuery(id+"F0.wireOp",EDGE,"E55.bottom"),sQuery(id+"F0.wireOp",EDGE,"E55.top"),sQuery(id+"F0.wireOp",EDGE,"E55.left"),sQuery(id+"F0.wireOp",EDGE,"E55.right")])],"isStart":false});
            var sketch = newSketch(context, id + "F17", { "sketchPlane" : qUnion([Q0])});
            skLineSegment(sketch, "E60", {"start": v(57.47, 58.74) * mm, "end": v(57.47, 56.2) * mm, "construction": true});
            skCircle(sketch, "E61", {"center": v(57.47, 57.47) * mm, "radius": 31.75 * mm});
            skCircle(sketch, "E62.MirrorC", {"center": v(57.47, -169.88) * mm, "radius": 31.75 * mm});
            skSolve(sketch);
        }
        {
            var Q0;
            Q0=makeQuery(id+"F15.opExtrude","CAP_FACE",FACE,{"disambiguationData":[OSD([sQuery(id+"F0.wireOp",EDGE,"E56.bottom"),sQuery(id+"F0.wireOp",EDGE,"E56.top"),sQuery(id+"F0.wireOp",EDGE,"E56.left"),sQuery(id+"F0.wireOp",EDGE,"E56.right")])],"isStart":false});
            var sketch = newSketch(context, id + "F18", { "sketchPlane" : qUnion([Q0])});
            skLineSegment(sketch, "E63", {"start": v(57.47, -56.2) * mm, "end": v(57.47, -58.74) * mm, "construction": true});
            skCircle(sketch, "E64", {"center": v(57.47, -57.47) * mm, "radius": 31.75 * mm});
            skSolve(sketch);
        }
        {
            var Q0;
            Q0=makeQuery(id+"F15.opExtrude","CAP_FACE",FACE,{"disambiguationData":[OSD([sQuery(id+"F0.wireOp",EDGE,"E57.bottom"),sQuery(id+"F0.wireOp",EDGE,"E57.top"),sQuery(id+"F0.wireOp",EDGE,"E57.left"),sQuery(id+"F0.wireOp",EDGE,"E57.right")])],"isStart":false});
            var sketch = newSketch(context, id + "F19", { "sketchPlane" : qUnion([Q0])});
            skLineSegment(sketch, "E65", {"start": v(-57.47, -56.2) * mm, "end": v(-57.47, -58.74) * mm, "construction": true});
            skCircle(sketch, "E66", {"center": v(-57.47, -57.47) * mm, "radius": 31.75 * mm});
            skSolve(sketch);
        }
        {
            var Q0;
            Q0=makeQuery(id+"F16.imprint","IMPRINT",FACE,{"disambiguationData":[TD([[makeQuery(id+"F16.imprint","IMPRINT",EDGE,{"derivedFrom":sQuery(id+"F16.wireOp",EDGE,"E59")}),1.0]])]});
            var Q1;
            Q1=makeQuery(id+"F17.imprint","IMPRINT",FACE,{"disambiguationData":[TD([[makeQuery(id+"F17.imprint","IMPRINT",EDGE,{"derivedFrom":sQuery(id+"F17.wireOp",EDGE,"E61")}),1.0]])]});
            var Q2;
            Q2=makeQuery(id+"F18.imprint","IMPRINT",FACE,{"disambiguationData":[TD([[makeQuery(id+"F18.imprint","IMPRINT",EDGE,{"derivedFrom":sQuery(id+"F18.wireOp",EDGE,"E64")}),1.0]])]});
            var Q3;
            Q3=makeQuery(id+"F19.imprint","IMPRINT",FACE,{"disambiguationData":[TD([[makeQuery(id+"F19.imprint","IMPRINT",EDGE,{"derivedFrom":sQuery(id+"F19.wireOp",EDGE,"E66")}),1.0]])]});
            extrude(context, id + "F20", {"entities" : qUnion([Q0, Q1, Q2, Q3]), "depth" : 2.54 * mm});
        }
    });
